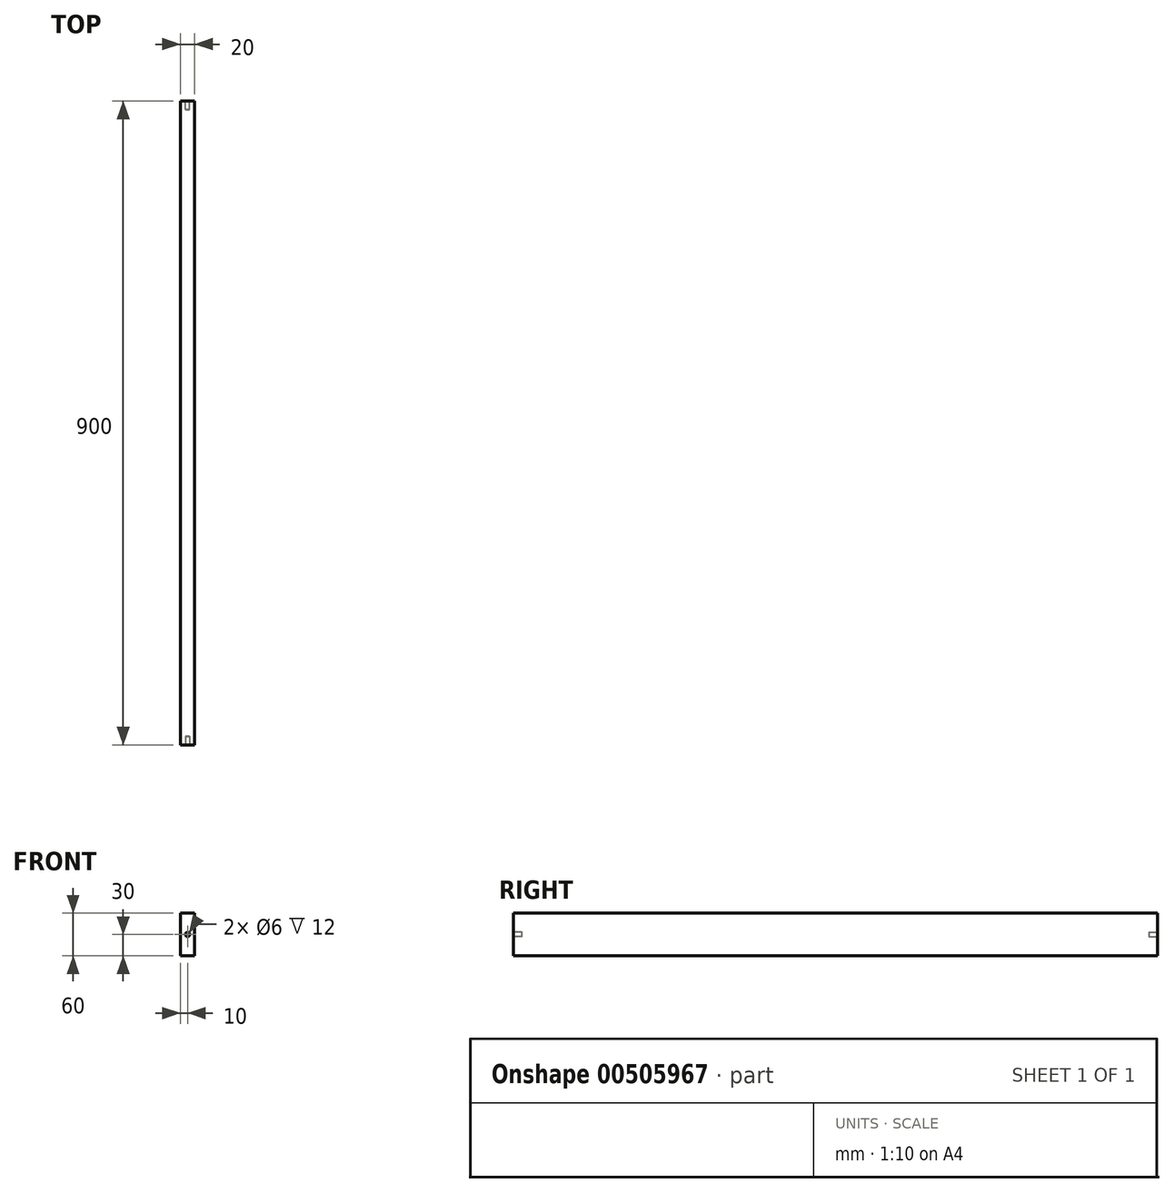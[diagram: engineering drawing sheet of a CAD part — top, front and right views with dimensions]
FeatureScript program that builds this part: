
annotation { "Feature Type Name" : "Feature", "Feature Type Description" : "" }
export const myFeature = defineFeature(function(context is Context, id is Id, definition is map)
    precondition{}
    {
        {
            var Q0;
            Q0=qCreatedBy(makeId("Front.planeOp"),FACE);
            var sketch = newSketch(context, id + "F0", { "sketchPlane" : qUnion([Q0])});
            skLineSegment(sketch, "E0.bottom", {"start": v(0, 0) * mm, "end": v(20, 0) * mm});
            skLineSegment(sketch, "E0.top", {"start": v(0, 60) * mm, "end": v(20, 60) * mm});
            skLineSegment(sketch, "E0.left", {"start": v(0, 0) * mm, "end": v(0, 60) * mm});
            skLineSegment(sketch, "E0.right", {"start": v(20, 0) * mm, "end": v(20, 60) * mm});
            skSolve(sketch);
        }
        {
            var Q0;
            Q0=makeQuery(id+"F0.imprint","IMPRINT",FACE,{"disambiguationData":[TD([[makeQuery(id+"F0.imprint","IMPRINT",EDGE,{"derivedFrom":sQuery(id+"F0.wireOp",EDGE,"E0.bottom")}),1.0]])]});
            extrude(context, id + "F1", {"entities" : qUnion([Q0]), "depth" : 900 * mm, "offsetDistance" : 25 * mm, "symmetric" : true});
        }
        {
            var Q0;
            Q0=makeQuery(id+"F1.opExtrude","CAP_FACE",FACE,{"disambiguationData":[OSD([sQuery(id+"F0.wireOp",EDGE,"E0.bottom"),sQuery(id+"F0.wireOp",EDGE,"E0.top"),sQuery(id+"F0.wireOp",EDGE,"E0.left"),sQuery(id+"F0.wireOp",EDGE,"E0.right")])],"isStart":false});
            var sketch = newSketch(context, id + "F2", { "sketchPlane" : qUnion([Q0])});
            skCircle(sketch, "E1", {"center": v(10, 30) * mm, "radius": 3 * mm});
            skSolve(sketch);
        }
        {
            var Q0;
            Q0=makeQuery(id+"F1.opExtrude","CAP_FACE",FACE,{"disambiguationData":[OSD([sQuery(id+"F0.wireOp",EDGE,"E0.bottom"),sQuery(id+"F0.wireOp",EDGE,"E0.top"),sQuery(id+"F0.wireOp",EDGE,"E0.left"),sQuery(id+"F0.wireOp",EDGE,"E0.right")])],"isStart":true});
            var sketch = newSketch(context, id + "F3", { "sketchPlane" : qUnion([Q0])});
            skCircle(sketch, "E2", {"center": v(-10, 30) * mm, "radius": 3 * mm});
            skSolve(sketch);
        }
        {
            var Q0;
            Q0=makeQuery(id+"F3.imprint","IMPRINT",FACE,{"disambiguationData":[TD([[makeQuery(id+"F3.imprint","IMPRINT",EDGE,{"derivedFrom":sQuery(id+"F3.wireOp",EDGE,"E2")}),1.0]])]});
            extrude(context, id + "F4", {"entities" : qUnion([Q0]), "operationType" : NewBodyOperationType.REMOVE, "oppositeDirection" : true, "depth" : 12 * mm, "offsetDistance" : 25 * mm});
        }
        {
            var Q0;
            Q0=makeQuery(id+"F2.imprint","IMPRINT",FACE,{"disambiguationData":[TD([[makeQuery(id+"F2.imprint","IMPRINT",EDGE,{"derivedFrom":sQuery(id+"F2.wireOp",EDGE,"E1")}),1.0]])]});
            extrude(context, id + "F5", {"entities" : qUnion([Q0]), "operationType" : NewBodyOperationType.REMOVE, "oppositeDirection" : true, "depth" : 12 * mm, "offsetDistance" : 25 * mm});
        }
    });
